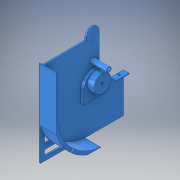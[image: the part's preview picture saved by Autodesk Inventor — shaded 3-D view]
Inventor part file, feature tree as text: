
AUTODESK INVENTOR PART (.ipt)
format: ipt  version: 2019 (Build 230136000, 136)  size: 510,464 bytes
history: native  units: in
note: dims shown in document units (in); Inventor stores cm internally (conversion verified against a paired STEP export)
features: extrude x25, sketch x24, chamfer x3, other x3, hole x2, pattern_linear x1, plane x1
ambient origin geometry x8: Origin, YZ Plane, XZ Plane, XY Plane, X Axis, Y Axis, Z Axis, Center Point
bodies: Solid1 (feature_tree)
feature tree (59):
  extrude  "Extrusion1"  Depth=6.6929in
  sketch  "Sketch2"  dims[d2=3.7402in d3=0.5in]
  hole  "Hole2"  [1 undecoded]
  hole  "Hole3"  [1 undecoded]
  pattern_linear  "Rectangular Pattern1"  Count1=2 Spacing1=0.3858in
  extrude  "Extrusion2"  TaperAngle=90.0deg  [1 undecoded]
  extrude  "Extrusion3"  Depth=3.7402in
  chamfer  "Chamfer1"  Distance=1.25in
  plane  "Work Plane1"
  extrude  "Extrusion7"  Depth=0.1181in TaperAngle=150.0deg
  extrude  "Extrusion8"  Depth=0.0787in
  other  "Work Axis1"
  extrude  "Extrusion11"  Depth=0.1181in
  other  "Work Point1"
  extrude  "Extrusion12"  Depth=0.3937in TaperAngle=0.0deg
  extrude  "Extrusion13"  Depth=0.1181in
  extrude  "Extrusion14"  Depth=0.1181in
  sketch  "Sketch20"  dims[d13=0.25in]
  other  "Work Point2"
  extrude  "Extrusion15"  Depth=0.9055in
  extrude  "Extrusion16"  Depth=0.122in TaperAngle=0.0deg
  extrude  "Extrusion17"  Depth=1.8898in
  extrude  "Extrusion18"  Depth=0.5906in
  extrude  "Extrusion19"  TaperAngle=90.0deg  [1 undecoded]
  extrude  "Extrusion20"  Depth=0.8661in
  sketch  "Sketch26"  dims[d29=0.1772in d30=0.75in d31=0.375in d32=0.25in d33=0.5635in d34=1.0in d35=0.8108in]
  extrude  "Extrusion21"  TaperAngle=90.0deg  [1 undecoded]
  extrude  "Extrusion22"  Depth=0.8661in
  chamfer  "Chamfer3"  [1 undecoded]
  extrude  "Extrusion23"  TaperAngle=180.0deg  [1 undecoded]
  extrude  "Extrusion24"  Depth=1.7323in
  extrude  "Extrusion25"  Depth=0.8661in
  extrude  "Extrusion26"  Depth=1.7323in
  extrude  "Extrusion27"  Depth=0.122in TaperAngle=0.0deg
  chamfer  "Chamfer4"  Distance=4.0754in
  extrude  "Extrusion28"  Depth=0.1181in
  extrude  "Extrusion29"  Depth=3.7402in
  extrude  "Extrusion30"  TaperAngle=90.0deg  [1 undecoded]
  sketch  "Sketch1"  dims[d0=6.6929in d1=4.5in]
  sketch  "Sketch3"  dims[d4=2.5669in d5=0.3858in]
  sketch  "Sketch4"  dims[d6=0.0in]
  sketch  "Sketch10"  dims[d8=2.5in]
  sketch  "Sketch11"  dims[d9=2.0in]
  sketch  "Sketch15"  dims[d10=3.7402in]
  sketch  "Sketch18"  dims[d11=3.7402in]
  sketch  "Sketch19"  dims[d12=4.0in]
  sketch  "Sketch21"  dims[d14=0.25in]
  sketch  "Sketch22"  dims[d17=0.1181in d18=0.0in]
  sketch  "Sketch23"  dims[d19=4.0in]
  sketch  "Sketch24"  dims[d20=3.7402in]
  sketch  "Sketch25"  dims[d21=2.9528in]
  sketch  "Sketch27"  dims[d36=0.1772in d37=0.75in d38=0.375in d39=0.25in d40=0.5635in d41=1.0in d42=0.8108in d43=0.7874in d45=0.3858in]
  sketch  "Sketch28"  dims[d46=2.0in d47=90.0deg]
  sketch  "Sketch29"  dims[d49=1.3681in d50=0.0in d51=3.7402in]
  sketch  "Sketch30"  dims[d52=3.7402in]
  sketch  "Sketch31"  dims[d53=3.7402in]
  sketch  "Sketch32"  dims[d54=180.0deg]
  sketch  "Sketch33"  dims[d55=90.0deg]
  sketch  "Sketch34"  dims[d56=4.0in d57=1.25in d58=0.0in d61=0.4in d62=0.125in d63=150.0deg d133=0.0787in d134=4.5276in d135=0.3937in d136=0.0in d137=0.2953in d138=0.2953in d139=0.9055in d140=0.122in d141=0.0in d143=1.8898in d166=0.5906in d167=90.0deg d168=0.8661in d169=90.0deg d170=0.8661in d171=0.0in d172=180.0deg d173=1.7323in d174=0.8661in d175=1.7323in d176=0.122in d177=0.0in d178=4.0754in d179=0.0in d180=3.7402in d181=90.0deg d182=0.5906in d183=90.0deg d185=0.0in d186=180.0deg d187=1.7323in d188=90.0deg d190=0.0in d191=180.0deg d192=0.9449in d193=90.0deg d194=1.8898in d195=90.0deg d196=1.8898in d197=0.0787in d198=0.8661in d199=180.0deg d200=180.0deg d201=0.9449in d202=180.0deg d203=180.0deg d204=0.25in d205=0.0in d218=0.8661in d219=0.0in d220=1.7323in d221=1.7323in d222=1.8898in d223=0.25in d224=0.0in d225=1.7323in d226=0.8661in d227=0.25in d228=0.0in d229=3.9967in d230=3.7402in d231=1.1811in d232=1.3386in d233=0.5in d234=0.0in d235=0.1772in d236=1.3386in d237=0.0492in d238=0.0in d239=1.7323in d240=1.1811in d241=1.3386in d242=0.0787in d243=0.0in d244=1.1811in d245=0.0787in d246=0.0in d247=1.1811in d248=0.0787in d249=0.0in d250=0.0984in d251=0.0787in d252=0.0in d253=1.1811in d254=90.0deg d255=0.2559in d256=0.374in d257=0.0787in d258=0.0in d259=0.75in d260=0.0in d261=0.0787in d262=0.0787in d263=45.0deg d264=0.472in d265=0.0in d267=0.3199in d268=0.0in d269=1.0in d270=0.0787in d271=0.0787in d272=180.0deg d273=5.5in d274=0.0in d275=0.81in d276=90.0deg d277=1.65in d278=180.0deg d279=0.1575in d280=0.3593in d281=0.0in d282=0.0787in d283=0.0in d284=0.315in d285=180.0deg d286=0.81in d287=90.0deg d288=0.1573in d289=180.0deg d290=0.1575in d291=2.3622in d292=0.315in d293=0.315in d294=0.1969in d295=0.3937in d296=0.1181in d297=0.0in d298=0.315in d299=0.81in d300=0.1573in d301=90.0deg d302=0.1575in d303=0.1181in d304=0.0in d305=0.1181in d306=0.0787in d307=45.0deg d308=0.1969in d309=0.0in d310=0.187in d311=1.055in d312=0.0787in d313=180.0deg d314=0.118in d315=0.1181in d316=0.1969in d317=0.0in d318=0.1772in d319=0.0886in d320=0.0886in d321=0.0886in d322=0.0886in d323=0.1181in d324=0.0in]
note: 8 required parameter values undecoded (feature->parameter linkage not recoverable at this tier; creation-order binding heuristic only, values carry confidence <= 0.55)
